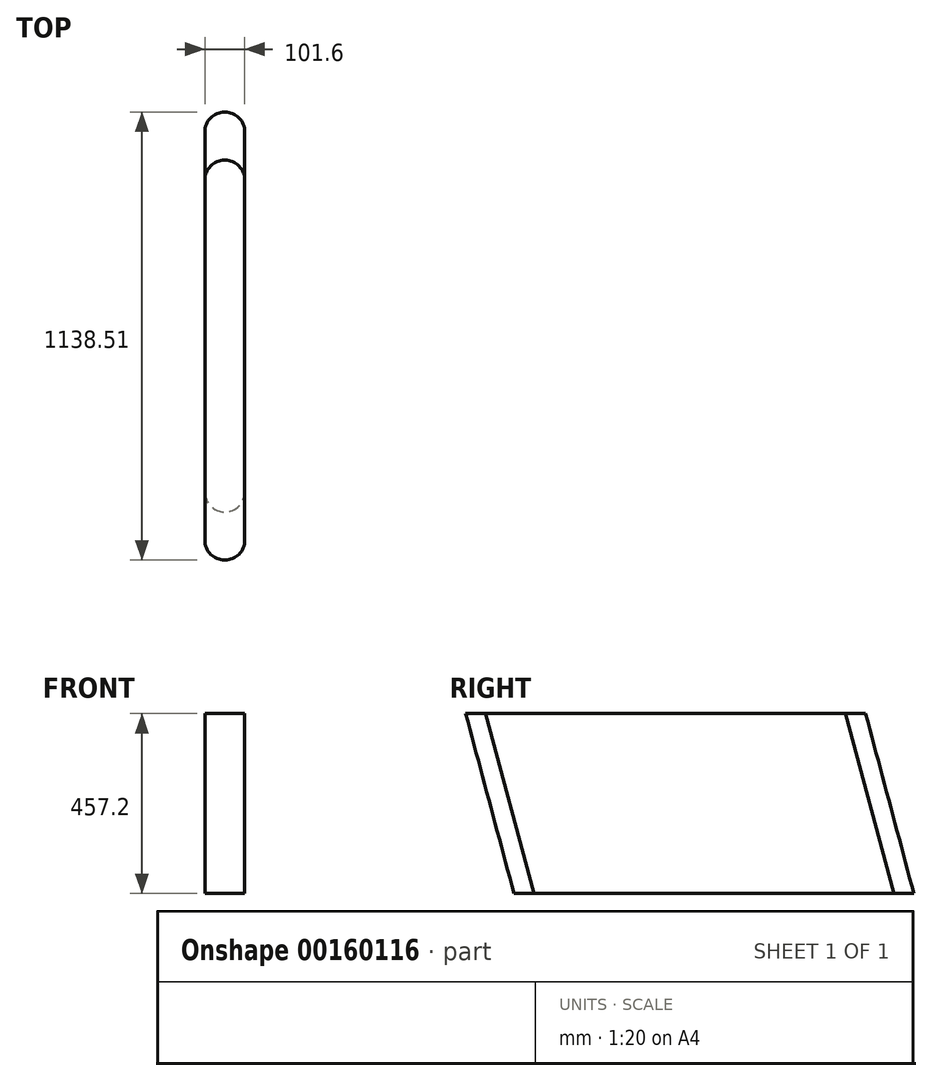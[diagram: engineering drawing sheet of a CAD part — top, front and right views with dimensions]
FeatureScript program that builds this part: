
annotation { "Feature Type Name" : "Feature", "Feature Type Description" : "" }
export const myFeature = defineFeature(function(context is Context, id is Id, definition is map)
    precondition{}
    {
        {
            var Q0;
            Q0=qCreatedBy(makeId("Top.planeOp"),FACE);
            var sketch = newSketch(context, id + "F0", { "sketchPlane" : qUnion([Q0])});
            skLineSegment(sketch, "E0.bottom", {"start": v(42.44, 992.28) * mm, "end": v(42.44, 992.28) * mm});
            skLineSegment(sketch, "E0.top", {"start": v(42.44, -23.72) * mm, "end": v(42.44, -23.72) * mm});
            skLineSegment(sketch, "E0.left", {"start": v(-8.36, 941.48) * mm, "end": v(-8.36, 27.08) * mm});
            skLineSegment(sketch, "E0.right", {"start": v(93.24, 941.48) * mm, "end": v(93.24, 27.08) * mm});
            skPoint(sketch, "E1.visualSharp", {"position": v(-8.36, 992.28) * mm});
            skArc(sketch, "E1.filletArc", {"start": v(42.44, 992.28) * mm, "mid": v(6.52, 977.4) * mm, "end": v(-8.36, 941.48) * mm});
            skPoint(sketch, "E2.visualSharp", {"position": v(93.24, 992.28) * mm});
            skArc(sketch, "E2.filletArc", {"start": v(93.24, 941.48) * mm, "mid": v(78.36, 977.4) * mm, "end": v(42.44, 992.28) * mm});
            skPoint(sketch, "E3.visualSharp", {"position": v(-8.36, -23.72) * mm});
            skArc(sketch, "E3.filletArc", {"start": v(-8.36, 27.08) * mm, "mid": v(6.52, -8.84) * mm, "end": v(42.44, -23.72) * mm});
            skPoint(sketch, "E4.visualSharp", {"position": v(93.24, -23.72) * mm});
            skArc(sketch, "E4.filletArc", {"start": v(42.44, -23.72) * mm, "mid": v(78.36, -8.84) * mm, "end": v(93.24, 27.08) * mm});
            skSolve(sketch);
        }
        {
            var Q0;
            Q0=qCreatedBy(makeId("Right.planeOp"),FACE);
            var sketch = newSketch(context, id + "F1", { "sketchPlane" : qUnion([Q0])});
            skLineSegment(sketch, "E5", {"start": v(0, 0) * mm, "end": v(-122.5, 457.2) * mm});
            skSolve(sketch);
        }
        {
            var Q0;
            Q0=makeQuery(id+"F0.imprint","IMPRINT",FACE,{"disambiguationData":[TD([[makeQuery(id+"F0.imprint","IMPRINT",EDGE,{"derivedFrom":sQuery(id+"F0.wireOp",EDGE,"E0.left")}),1.0]])]});
            var Q1;
            Q1=sQuery(id+"F1.wireOp",EDGE,"E5");
            sweep(context, id + "F2", {"profiles" : qUnion([Q0]), "path" : qUnion([Q1])});
        }
    });
